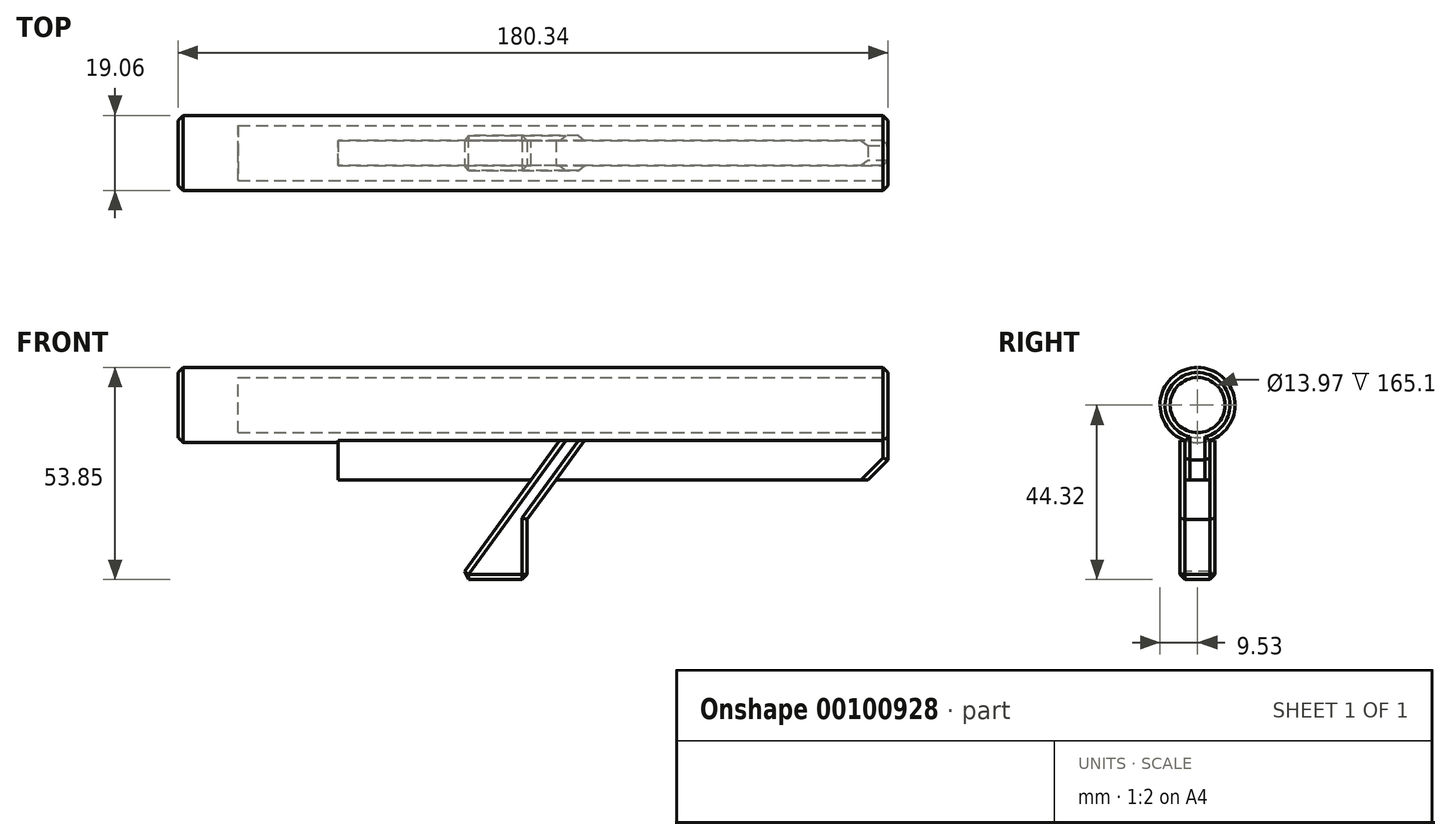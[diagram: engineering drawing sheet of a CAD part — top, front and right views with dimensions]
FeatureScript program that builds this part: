
annotation { "Feature Type Name" : "Feature", "Feature Type Description" : "" }
export const myFeature = defineFeature(function(context is Context, id is Id, definition is map)
    precondition{}
    {
        {
            var Q0;
            Q0=qCreatedBy(makeId("Right.planeOp"),FACE);
            var sketch = newSketch(context, id + "F0", { "sketchPlane" : qUnion([Q0])});
            skCircle(sketch, "E0", {"center": v(0, 0) * mm, "radius": 9.53 * mm});
            skSolve(sketch);
        }
        {
            var Q0;
            Q0 = qSketchRegion(id + "F0", true);
            extrude(context, id + "F1", {"entities" : qUnion([Q0]), "depth" : 180.34 * mm});
        }
        {
            var Q0;
            Q0=makeQuery(id+"F1.opExtrude","CAP_FACE",FACE,{"disambiguationData":[OSD([sQuery(id+"F0.wireOp",EDGE,"E0")])],"isStart":false});
            var sketch = newSketch(context, id + "F2", { "sketchPlane" : qUnion([Q0])});
            skLineSegment(sketch, "E1", {"start": v(0, 0) * mm, "end": v(3.18, 0) * mm});
            skLineSegment(sketch, "E2", {"start": v(3.18, 0) * mm, "end": v(3.18, -19.05) * mm});
            skLineSegment(sketch, "E3", {"start": v(3.18, -19.05) * mm, "end": v(-3.17, -19.05) * mm});
            skLineSegment(sketch, "E4", {"start": v(-3.17, -19.05) * mm, "end": v(-3.18, 0) * mm});
            skLineSegment(sketch, "E5", {"start": v(-3.18, 0) * mm, "end": v(0, 0) * mm});
            skSolve(sketch);
        }
        {
            var Q0;
            Q0 = qSketchRegion(id + "F2", true);
            extrude(context, id + "F3", {"entities" : qUnion([Q0]), "operationType" : NewBodyOperationType.ADD, "oppositeDirection" : true, "depth" : 139.7 * mm});
        }
        {
            var Q0;
            Q0=makeQuery(id+"F1.opExtrude","CAP_FACE",FACE,{"disambiguationData":[OSD([sQuery(id+"F0.wireOp",EDGE,"E0")])],"isStart":false});
            var sketch = newSketch(context, id + "F4", { "sketchPlane" : qUnion([Q0])});
            skCircle(sketch, "E6", {"center": v(0, 0) * mm, "radius": 6.99 * mm});
            skSolve(sketch);
        }
        {
            var Q0;
            Q0 = qSketchRegion(id + "F4", true);
            extrude(context, id + "F5", {"entities" : qUnion([Q0]), "operationType" : NewBodyOperationType.REMOVE, "oppositeDirection" : true, "depth" : 165.1 * mm});
        }
        {
            var Q0;
            Q0=makeQuery(id+"F3.opExtrude","CAP_EDGE",EDGE,{"disambiguationData":[OSD([sQuery(id+"F2.wireOp",EDGE,"E3")])],"isStart":true});
            chamfer(context, id + "F6", {"entities" : qUnion([Q0]), "width" : 5.08 * mm, "tangentPropagation" : true});
        }
        {
            var Q0;
            Q0=makeQuery(id+"F1.opExtrude","CAP_EDGE",EDGE,{"disambiguationData":[OSD([sQuery(id+"F0.wireOp",EDGE,"E0")])],"isStart":false});
            var Q1;
            Q1=makeQuery(id+"F3.opExtrude","CAP_EDGE",EDGE,{"disambiguationData":[OSD([sQuery(id+"F2.wireOp",EDGE,"E4")])],"isStart":true});
            var Q2;
            Q2=makeQuery(id+"F3.opExtrude","CAP_EDGE",EDGE,{"disambiguationData":[OSD([sQuery(id+"F2.wireOp",EDGE,"E2")])],"isStart":true});
            var Q3;
            Q3=makeQuery(id+"F6.opChamfer","BLEND_EDGE",EDGE,{"blendedFrom":[makeQuery(id+"F3.opExtrude","CAP_EDGE",EDGE,{"disambiguationData":[OSD([sQuery(id+"F2.wireOp",EDGE,"E3")])],"isStart":true}),makeQuery(id+"F3.opExtrude","SWEPT_FACE",FACE,{"disambiguationData":[OSD([sQuery(id+"F2.wireOp",EDGE,"E4")])]})],"blendedInto":[makeQuery(id+"F3.opExtrude","SWEPT_FACE",FACE,{"disambiguationData":[OSD([sQuery(id+"F2.wireOp",EDGE,"E4")])]})]});
            var Q4;
            Q4=makeQuery(id+"F6.opChamfer","BLEND_EDGE",EDGE,{"blendedFrom":[makeQuery(id+"F3.opExtrude","CAP_EDGE",EDGE,{"disambiguationData":[OSD([sQuery(id+"F2.wireOp",EDGE,"E3")])],"isStart":true}),makeQuery(id+"F3.opExtrude","SWEPT_FACE",FACE,{"disambiguationData":[OSD([sQuery(id+"F2.wireOp",EDGE,"E2")])]})],"blendedInto":[makeQuery(id+"F3.opExtrude","SWEPT_FACE",FACE,{"disambiguationData":[OSD([sQuery(id+"F2.wireOp",EDGE,"E2")])]})]});
            var Q5;
            Q5=makeQuery(id+"F1.opExtrude","CAP_EDGE",EDGE,{"disambiguationData":[OSD([sQuery(id+"F0.wireOp",EDGE,"E0")])],"isStart":true});
            chamfer(context, id + "F7", {"entities" : qUnion([Q0, Q1, Q2, Q3, Q4, Q5]), "width" : 1.27 * mm, "tangentPropagation" : true});
        }
        {
            var Q0;
            Q0=makeQuery(id+"F3.opExtrude","SWEPT_FACE",FACE,{"disambiguationData":[OSD([sQuery(id+"F2.wireOp",EDGE,"E4")])]});
            var sketch = newSketch(context, id + "F8", { "sketchPlane" : qUnion([Q0])});
            skLineSegment(sketch, "E7", {"start": v(96, -19.05) * mm, "end": v(88.68, -29.12) * mm});
            skLineSegment(sketch, "E8", {"start": v(88.68, -29.12) * mm, "end": v(88.68, -44.32) * mm});
            skLineSegment(sketch, "E9", {"start": v(88.68, -44.32) * mm, "end": v(83.6, -44.32) * mm});
            skLineSegment(sketch, "E10", {"start": v(83.62, -27.34) * mm, "end": v(89.64, -19.05) * mm});
            skLineSegment(sketch, "E11", {"start": v(89.64, -19.05) * mm, "end": v(96, -19.05) * mm, "construction": true});
            skLineSegment(sketch, "E12", {"start": v(89.64, -19.05) * mm, "end": v(96, -19.05) * mm});
            skLineSegment(sketch, "E13", {"start": v(89.64, -19.05) * mm, "end": v(96.96, -8.98) * mm});
            skLineSegment(sketch, "E14", {"start": v(96.96, -8.98) * mm, "end": v(103.31, -8.98) * mm});
            skLineSegment(sketch, "E15", {"start": v(103.31, -8.98) * mm, "end": v(96, -19.05) * mm});
            skLineSegment(sketch, "E16", {"start": v(83.62, -27.34) * mm, "end": v(71.28, -44.32) * mm});
            skLineSegment(sketch, "E17", {"start": v(71.28, -44.32) * mm, "end": v(83.6, -44.32) * mm});
            skSolve(sketch);
        }
        {
            var Q0;
            Q0 = qSketchRegion(id + "F8", true);
            var Q1;
            Q1=makeQuery(id+"F3.opExtrude","SWEPT_FACE",FACE,{"disambiguationData":[OSD([sQuery(id+"F2.wireOp",EDGE,"E2")])]});
            extrude(context, id + "F9", {"entities" : qUnion([Q0]), "operationType" : NewBodyOperationType.ADD, "oppositeDirection" : true, "endBoundEntityFace" : qUnion([Q1]), "depth" : 7.62 * mm, "hasSecondDirection" : true, "secondDirectionOppositeDirection" : false, "secondDirectionDepth" : 1.27 * mm});
        }
        {
            var Q0;
            Q0=makeQuery(id+"F9.opExtrude","CAP_EDGE",EDGE,{"disambiguationData":[OSD([sQuery(id+"F8.wireOp",EDGE,"E8")])],"isStart":true});
            var Q1;
            Q1=makeQuery(id+"F9.opExtrude","CAP_EDGE",EDGE,{"disambiguationData":[OSD([sQuery(id+"F8.wireOp",EDGE,"E8")])],"isStart":false});
            var Q2;
            Q2=makeQuery(id+"F9.opExtrude","CAP_EDGE",EDGE,{"disambiguationData":[OSD([sQuery(id+"F8.wireOp",EDGE,"E7"),sQuery(id+"F8.wireOp",EDGE,"E15")])],"isStart":true});
            var Q3;
            Q3=makeQuery(id+"F9.opExtrude","CAP_EDGE",EDGE,{"disambiguationData":[OSD([sQuery(id+"F8.wireOp",EDGE,"E10"),sQuery(id+"F8.wireOp",EDGE,"E13")])],"isStart":true});
            var Q4;
            Q4=makeQuery(id+"F9.opExtrude","CAP_EDGE",EDGE,{"disambiguationData":[OSD([sQuery(id+"F8.wireOp",EDGE,"E10"),sQuery(id+"F8.wireOp",EDGE,"E13")])],"isStart":false});
            var Q5;
            Q5=makeQuery(id+"F9.opExtrude","CAP_EDGE",EDGE,{"disambiguationData":[OSD([sQuery(id+"F8.wireOp",EDGE,"PpPLshaK-i5t3-6q67-NNYp-Fj0mDHfWlRCz")])],"isStart":true});
            var Q6;
            Q6=makeQuery(id+"F9.opExtrude","SWEPT_FACE",FACE,{"disambiguationData":[OSD([sQuery(id+"F8.wireOp",EDGE,"E9")])]});
            var Q7;
            Q7=makeQuery(id+"F9.opExtrude","CAP_EDGE",EDGE,{"disambiguationData":[OSD([sQuery(id+"F8.wireOp",EDGE,"PpPLshaK-i5t3-6q67-NNYp-Fj0mDHfWlRCz")])],"isStart":false});
            var Q8;
            Q8=makeQuery(id+"F9.opExtrude","CAP_EDGE",EDGE,{"disambiguationData":[OSD([sQuery(id+"F8.wireOp",EDGE,"E7"),sQuery(id+"F8.wireOp",EDGE,"E15")])],"isStart":false});
            chamfer(context, id + "F10", {"entities" : qUnion([Q0, Q1, Q2, Q3, Q4, Q5, Q6, Q7, Q8]), "width" : 1.27 * mm, "tangentPropagation" : true});
        }
    });
